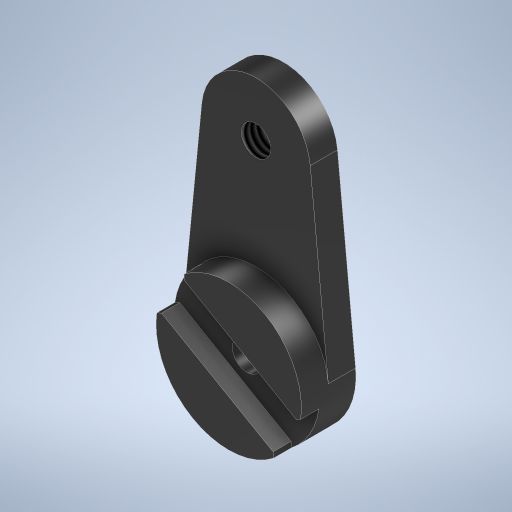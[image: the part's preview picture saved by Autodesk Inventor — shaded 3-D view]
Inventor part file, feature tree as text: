
AUTODESK INVENTOR PART (.ipt)
format: ipt  version: 2024.2 (Build 282272000, 272)  size: 291,840 bytes
history: native  units: mm
features: other x3, chamfer x1
ambient origin geometry x8: Origin, YZ Plane, XZ Plane, XY Plane, X Axis, Y Axis, Z Axis, Center Point
bodies: Solid1 (feature_tree)
feature tree (4):
  other  "LongCrankFrameBasis.ipt"
  chamfer  "C0.5"  Distance=10.0mm
  other  "Solid1::LongCrankFrameBasis.ipt"
  other  "TaggingFeature1"
